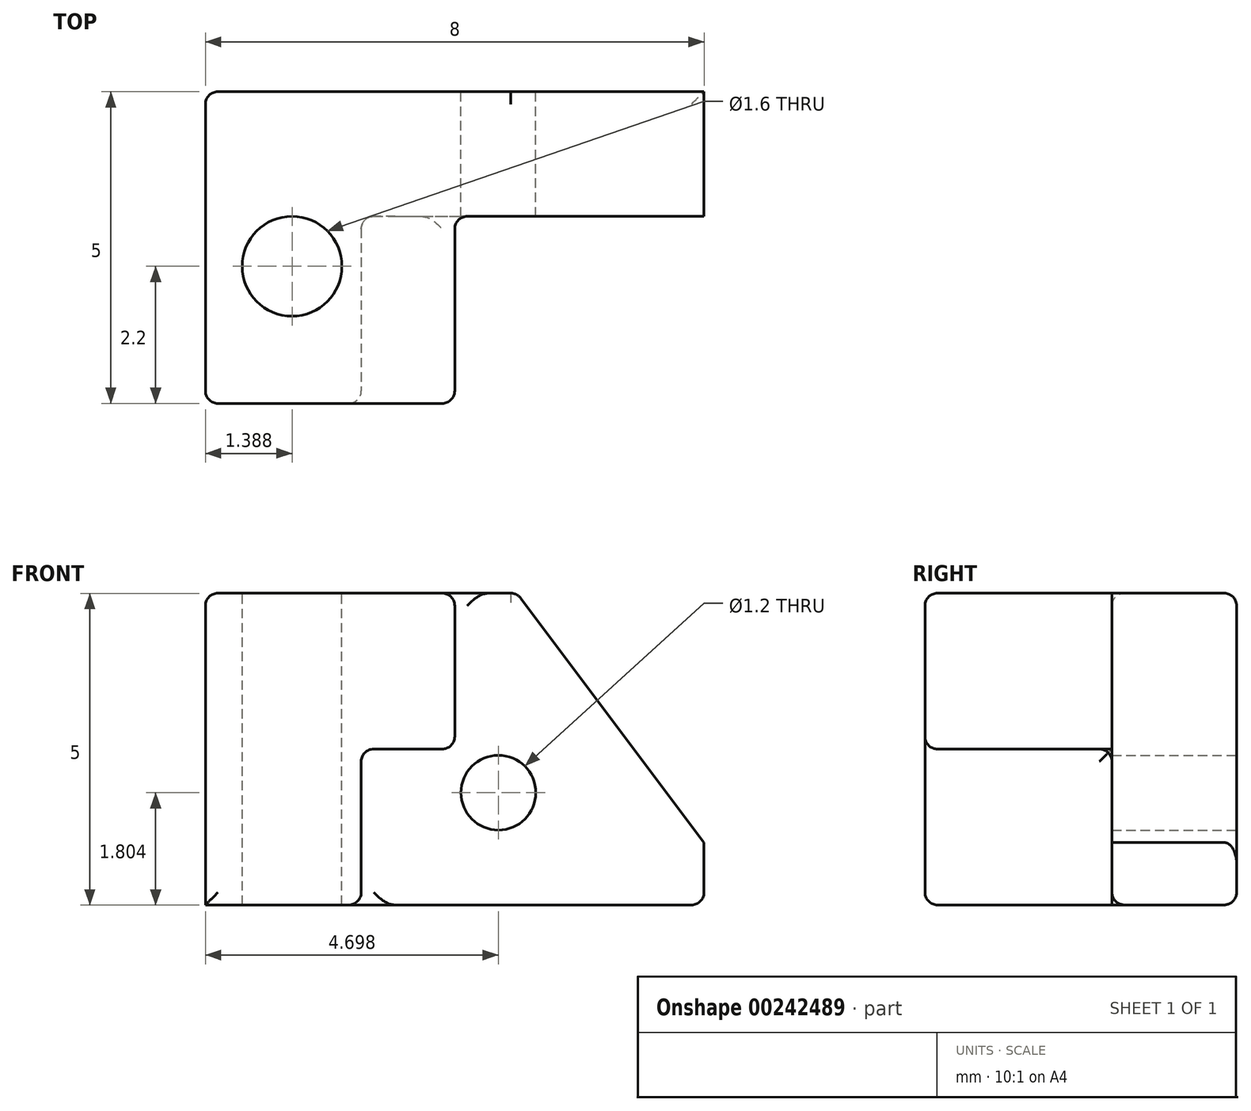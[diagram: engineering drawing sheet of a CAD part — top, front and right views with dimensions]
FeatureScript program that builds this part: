
annotation { "Feature Type Name" : "Feature", "Feature Type Description" : "" }
export const myFeature = defineFeature(function(context is Context, id is Id, definition is map)
    precondition{}
    {
        {
            var Q0;
            Q0=qCreatedBy(makeId("Front.planeOp"),FACE);
            var sketch = newSketch(context, id + "F0", { "sketchPlane" : qUnion([Q0])});
            skLineSegment(sketch, "E0.bottom", {"start": v(-4.38, 6.2) * mm, "end": v(3.62, 6.2) * mm});
            skLineSegment(sketch, "E0.top", {"start": v(-4.38, 1.2) * mm, "end": v(3.62, 1.2) * mm});
            skLineSegment(sketch, "E0.left", {"start": v(-4.38, 6.2) * mm, "end": v(-4.38, 1.2) * mm});
            skLineSegment(sketch, "E0.right", {"start": v(3.62, 6.2) * mm, "end": v(3.62, 1.2) * mm});
            skSolve(sketch);
        }
        {
            var Q0;
            Q0=makeQuery(id+"F0.imprint","IMPRINT",FACE,{"disambiguationData":[TD([[makeQuery(id+"F0.imprint","IMPRINT",EDGE,{"derivedFrom":sQuery(id+"F0.wireOp",EDGE,"E0.bottom")}),-1.0]])]});
            extrude(context, id + "F1", {"entities" : qUnion([Q0]), "depth" : 5 * mm});
        }
        {
            var Q0;
            Q0=makeQuery(id+"F1.opExtrude","CAP_FACE",FACE,{"disambiguationData":[OSD([sQuery(id+"F0.wireOp",EDGE,"E0.bottom"),sQuery(id+"F0.wireOp",EDGE,"E0.top"),sQuery(id+"F0.wireOp",EDGE,"E0.left"),sQuery(id+"F0.wireOp",EDGE,"E0.right")])],"isStart":false});
            var sketch = newSketch(context, id + "F2", { "sketchPlane" : qUnion([Q0])});
            skLineSegment(sketch, "E1", {"start": v(-4.38, 6.2) * mm, "end": v(-0.38, 6.2) * mm});
            skLineSegment(sketch, "E2", {"start": v(-4.38, 6.2) * mm, "end": v(-4.38, 1.2) * mm});
            skLineSegment(sketch, "E3", {"start": v(-4.38, 1.2) * mm, "end": v(-1.88, 1.2) * mm});
            skLineSegment(sketch, "E4", {"start": v(-1.88, 1.2) * mm, "end": v(-1.88, 3.7) * mm});
            skLineSegment(sketch, "E5", {"start": v(-1.88, 3.7) * mm, "end": v(-0.38, 3.7) * mm});
            skLineSegment(sketch, "E6", {"start": v(-0.38, 3.7) * mm, "end": v(-0.38, 6.2) * mm});
            skSolve(sketch);
        }
        {
            var Q0;
            {var subQ3=sQuery(id+"F2.wireOp",EDGE,"E4");Q0=makeQuery(id+"F2.imprint","IMPRINT",FACE,{"disambiguationData":[TD([[makeQuery(id+"F2.imprint","IMPRINT",EDGE,{"derivedFrom":subQ3}),-1.0]])]});}
            extrude(context, id + "F3", {"entities" : qUnion([Q0]), "operationType" : NewBodyOperationType.REMOVE, "oppositeDirection" : true, "depth" : 3 * mm});
        }
        {
            var Q0;
            Q0=makeQuery(id+"F1.opExtrude","SWEPT_EDGE",EDGE,{"disambiguationData":[OSD([sQuery(id+"F0.wireOp",EDGE,"E0.bottom"),sQuery(id+"F0.wireOp",EDGE,"E0.right")])]});
            chamfer(context, id + "F4", {"entities" : qUnion([Q0]), "chamferType" : ChamferType.TWO_OFFSETS, "width1" : 3 * mm, "oppositeDirection" : false, "width2" : 4 * mm, "tangentPropagation" : true});
        }
        {
            var Q0;
            Q0=makeQuery(id+"F3.boolean.opBoolean","COPY",EDGE,{"derivedFrom":makeQuery(id+"F3.opExtrude","SWEPT_EDGE",EDGE,{"disambiguationData":[OSD([sQuery(id+"F0.wireOp",EDGE,"E0.bottom"),sQuery(id+"F2.wireOp",EDGE,"E1"),sQuery(id+"F2.wireOp",EDGE,"E6")])]})});
            var Q1;
            Q1=makeQuery(id+"F1.opExtrude","CAP_EDGE",EDGE,{"disambiguationData":[OSD([sQuery(id+"F0.wireOp",EDGE,"E0.bottom")])],"isStart":false});
            var Q2;
            Q2=makeQuery(id+"F1.opExtrude","CAP_EDGE",EDGE,{"disambiguationData":[OSD([sQuery(id+"F0.wireOp",EDGE,"E0.bottom")])],"isStart":true});
            var Q3;
            Q3=makeQuery(id+"F1.opExtrude","SWEPT_EDGE",EDGE,{"disambiguationData":[OSD([sQuery(id+"F0.wireOp",EDGE,"E0.bottom"),sQuery(id+"F0.wireOp",EDGE,"E0.left")])]});
            var Q4;
            Q4=makeQuery(id+"F1.opExtrude","CAP_FACE",FACE,{"disambiguationData":[OSD([sQuery(id+"F0.wireOp",EDGE,"E0.bottom"),sQuery(id+"F0.wireOp",EDGE,"E0.top"),sQuery(id+"F0.wireOp",EDGE,"E0.left"),sQuery(id+"F0.wireOp",EDGE,"E0.right")])],"isStart":false});
            var Q5;
            Q5=makeQuery(id+"F3.boolean.opBoolean","COPY",FACE,{"derivedFrom":makeQuery(id+"F3.opExtrude","SWEPT_FACE",FACE,{"disambiguationData":[OSD([sQuery(id+"F2.wireOp",EDGE,"E6")])]})});
            var Q6;
            Q6=makeQuery(id+"F3.boolean.opBoolean","COPY",FACE,{"derivedFrom":makeQuery(id+"F3.opExtrude","SWEPT_FACE",FACE,{"disambiguationData":[OSD([sQuery(id+"F2.wireOp",EDGE,"E4")])]})});
            var Q7;
            Q7=makeQuery(id+"F3.boolean.opBoolean","COPY",EDGE,{"derivedFrom":makeQuery(id+"F3.opExtrude","CAP_EDGE",EDGE,{"disambiguationData":[OSD([sQuery(id+"F0.wireOp",EDGE,"E0.top")])],"isStart":false})});
            var Q8;
            Q8=makeQuery(id+"F1.opExtrude","SWEPT_EDGE",EDGE,{"disambiguationData":[OSD([sQuery(id+"F0.wireOp",EDGE,"E0.top"),sQuery(id+"F0.wireOp",EDGE,"E0.right")])]});
            var Q9;
            Q9=makeQuery(id+"F1.opExtrude","CAP_EDGE",EDGE,{"disambiguationData":[OSD([sQuery(id+"F0.wireOp",EDGE,"E0.top")])],"isStart":true});
            var Q10;
            Q10=makeQuery(id+"F1.opExtrude","CAP_EDGE",EDGE,{"disambiguationData":[OSD([sQuery(id+"F0.wireOp",EDGE,"E0.left")])],"isStart":true});
            fillet(context, id + "F5", {"entities" : qUnion([Q0, Q1, Q2, Q3, Q4, Q5, Q6, Q7, Q8, Q9, Q10]), "radius" : 0.2 * mm, "tangentPropagation" : true, "allowEdgeOverflow" : false});
        }
        {
            var Q0;
            Q0=qCreatedBy(makeId("Front.planeOp"),FACE);
            var sketch = newSketch(context, id + "F6", { "sketchPlane" : qUnion([Q0])});
            skCircle(sketch, "E7", {"center": v(0.32, 3) * mm, "radius": 0.6 * mm});
            skSolve(sketch);
        }
        {
            var Q0;
            Q0=makeQuery(id+"F6.imprint","IMPRINT",FACE,{"disambiguationData":[TD([[makeQuery(id+"F6.imprint","IMPRINT",EDGE,{"derivedFrom":sQuery(id+"F6.wireOp",EDGE,"E7")}),1.0]])]});
            var Q1;
            Q1=makeQuery(id+"F3.boolean.opBoolean","COPY",FACE,{"derivedFrom":makeQuery(id+"F3.opExtrude","CAP_FACE",FACE,{"disambiguationData":[OSD([sQuery(id+"F0.wireOp",EDGE,"E0.bottom"),sQuery(id+"F0.wireOp",EDGE,"E0.top"),sQuery(id+"F0.wireOp",EDGE,"E0.right"),sQuery(id+"F2.wireOp",EDGE,"E4"),sQuery(id+"F2.wireOp",EDGE,"E5"),sQuery(id+"F2.wireOp",EDGE,"E6")])],"isStart":false})});
            extrude(context, id + "F7", {"entities" : qUnion([Q0]), "operationType" : NewBodyOperationType.REMOVE, "endBound" : BoundingType.UP_TO_SURFACE, "endBoundEntityFace" : qUnion([Q1]), "depth" : 25 * mm});
        }
        {
            var Q0;
            Q0=makeQuery(id+"F1.opExtrude","SWEPT_FACE",FACE,{"disambiguationData":[OSD([sQuery(id+"F0.wireOp",EDGE,"E0.bottom")])]});
            var sketch = newSketch(context, id + "F8", { "sketchPlane" : qUnion([Q0])});
            skCircle(sketch, "E8", {"center": v(-3, -2.8) * mm, "radius": 0.8 * mm});
            skSolve(sketch);
        }
        {
            var Q0;
            Q0 = qSketchRegion(id + "F8", true);
            var Q1;
            Q1=makeQuery(id+"F1.opExtrude","SWEPT_FACE",FACE,{"disambiguationData":[OSD([sQuery(id+"F0.wireOp",EDGE,"E0.top")])]});
            extrude(context, id + "F9", {"entities" : qUnion([Q0]), "operationType" : NewBodyOperationType.REMOVE, "endBound" : BoundingType.UP_TO_SURFACE, "oppositeDirection" : true, "endBoundEntityFace" : qUnion([Q1]), "depth" : 25 * mm});
        }
        {
            var Q0;
            {var subQ0=sQuery(id+"F0.wireOp",EDGE,"E0.bottom");Q0=makeQuery(id+"F4.opChamfer","BLEND_EDGE",EDGE,{"blendedFrom":[makeQuery(id+"F1.opExtrude","SWEPT_EDGE",EDGE,{"disambiguationData":[OSD([subQ0,sQuery(id+"F0.wireOp",EDGE,"E0.right")])]}),makeQuery(id+"F1.opExtrude","SWEPT_FACE",FACE,{"disambiguationData":[OSD([subQ0])]})],"blendedInto":[makeQuery(id+"F1.opExtrude","SWEPT_FACE",FACE,{"disambiguationData":[OSD([subQ0])]})]});}
            fillet(context, id + "F10", {"entities" : qUnion([Q0]), "radius" : 0.2 * mm, "tangentPropagation" : true, "allowEdgeOverflow" : false});
        }
    });
